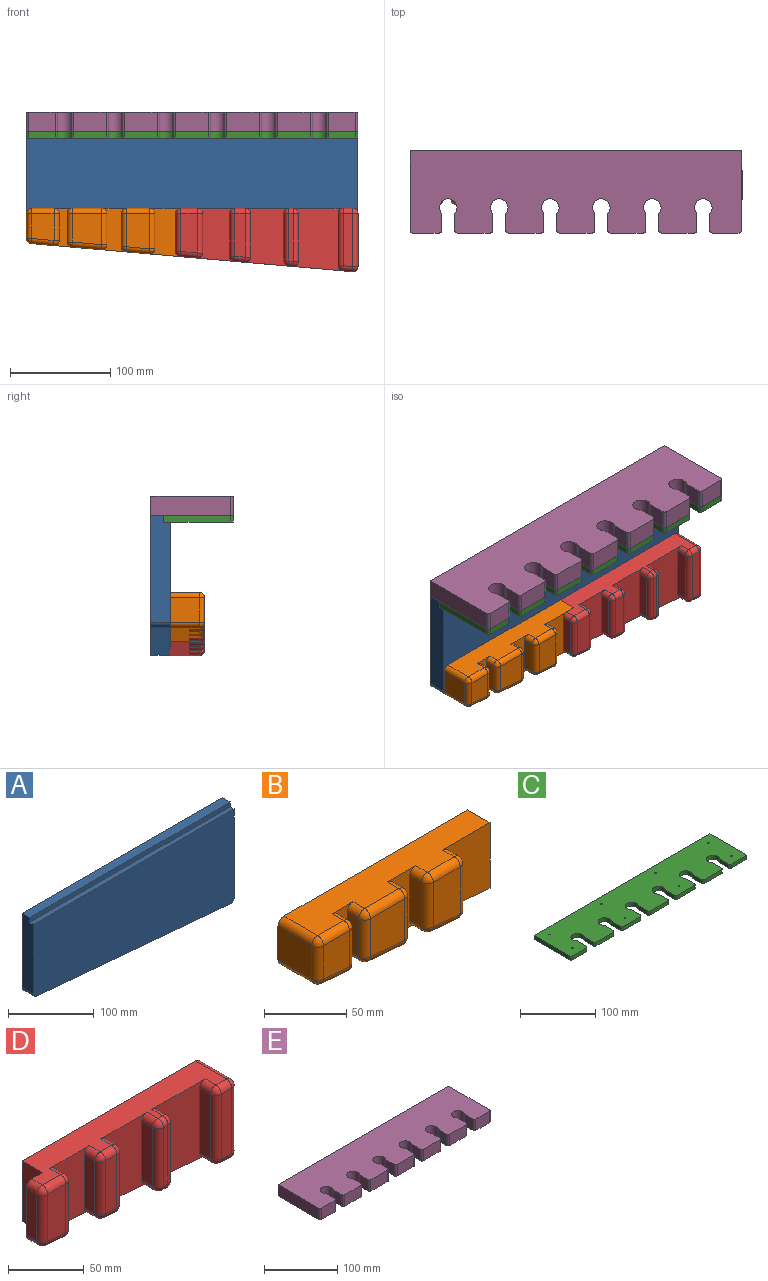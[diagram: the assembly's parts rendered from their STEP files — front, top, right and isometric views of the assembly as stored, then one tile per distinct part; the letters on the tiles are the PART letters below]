
ASSEMBLY  parts=5 mates=3
PART A: 10 faces, bbox 330.2x19.1x139.2 mm
  f0: plane 106.16x19.05mm, normal (-1,0,0), area 1978.7mm2, adj f2,f3,f4,f5,f6,f8
  f1: plane 134.16x19.05mm, normal (1,0,0), area 2512.1mm2, adj f2,f3,f4,f5,f6,f9
  f2: plane 330.2x12.7mm, normal (0,0,1), area 4193.5mm2, adj f0,f1,f3,f6
  f3: plane 330.2x139.24mm, normal (0,1,0), area 41348.1mm2, adj f0,f1,f2,f7,f8,f9
  f4: plane 330.2x132.38mm, normal (0,-1,0), area 39083.6mm2, adj f0,f1,f5,f7,f8,f9
  f5: plane 330.2x6.35mm, normal (0,0,1), area 2096.8mm2, adj f0,f1,f4,f6
  f6: plane 330.2x6.86mm, normal (0,-1,0), area 2264.5mm2, adj f0,f1,f2,f5
  f7: plane 320.04x28mm, normal (-0.09,0,-1), area 6120.1mm2, adj f3,f4,f8,f9
  f8: cylinder r=5.08mm len=19.05mm, axis (0,1,0), area 143.6mm2, adj f0,f3,f4,f7
  f9: cylinder r=5.08mm len=19.05mm, axis (0,-1,0), area 160.5mm2, adj f1,f3,f4,f7
PART B: 60 faces, bbox 163.5x34.1x48.9 mm
  f0: plane 29.06x24.88mm, normal (-1,0,0), area 722.8mm2, adj f6,f40,f42,f43
  f1: plane 48.92x19.05mm, normal (1,0,0), area 931.9mm2, adj f5,f6,f14,f15
  f2: plane 35.17x23.24mm, normal (0,-1,0), area 793.8mm2, adj f31,f32,f36,f37
  f3: plane 26.84x22.42mm, normal (0,-1,0), area 579.6mm2, adj f43,f44,f48,f49
  f4: plane 31x29.59mm, normal (0,-1,0), area 879.1mm2, adj f19,f20,f24,f25
  f5: plane 158.43x29.06mm, normal (0,0,1), area 3771.2mm2, adj f1,f6,f9,f12,f14,f16,f20,f21
  f6: plane 163.51x48.92mm, normal (0,1,0), area 6803.7mm2, adj f0,f1,f5,f15,f40,f42,f52,f54
  f7: plane 31x10.01mm, normal (1,0,0), area 310.3mm2, adj f9,f21,f25,f27
  f8: plane 33.14x10.01mm, normal (-1,0,0), area 331.6mm2, adj f9,f30,f36,f39
  f9: plane 43.28x24.83mm, normal (0,-1,0), area 623.3mm2, adj f5,f7,f8,f15,f21,f27,f30,f39
  f10: plane 26.84x10.01mm, normal (1,0,0), area 268.6mm2, adj f12,f45,f49,f51
  f11: plane 28.42x10.01mm, normal (-1,0,0), area 284.4mm2, adj f12,f16,f18,f19
  f12: plane 38.56x18.48mm, normal (0,-1,0), area 320mm2, adj f5,f10,f11,f15,f16,f18,f45,f51
  f13: plane 35.17x10.01mm, normal (1,0,0), area 352mm2, adj f14,f28,f32,f33
  f14: plane 48.92x41.21mm, normal (0,-1,0), area 1702.3mm2, adj f1,f5,f13,f15,f28,f33
  f15: plane 158.88x29.06mm, normal (-0.09,0,-1), area 3794.1mm2, adj f1,f6,f9,f12,f14,f18,f24,f27
  f16: cylinder r=5.08mm len=10.01mm, axis (0,1,0), area 79.9mm2, adj f5,f11,f12,f17
  f17: sphere r=5.08mm, area 40.5mm2, adj f16,f19,f20
  f18: cylinder r=5.08mm len=10.01mm, axis (0,-1,0), area 75.4mm2, adj f11,f12,f15,f22
  f19: cylinder r=5.08mm len=28.42mm, axis (0,0,-1), area 226.7mm2, adj f4,f11,f17,f22
  f20: cylinder r=5.08mm len=29.59mm, axis (-1,0,0), area 236.1mm2, adj f4,f5,f17,f23
  f21: cylinder r=5.08mm len=10.01mm, axis (0,1,0), area 79.9mm2, adj f5,f7,f9,f23
  f22: sphere r=5.08mm, area 38.3mm2, adj f18,f19,f24
  f23: sphere r=5.08mm, area 40.5mm2, adj f20,f21,f25
  f24: cylinder r=5.08mm len=30.03mm, axis (1,0,-0.09), area 237mm2, adj f4,f15,f22,f26
  f25: cylinder r=5.08mm len=31mm, axis (0,0,1), area 247.4mm2, adj f4,f7,f23,f26
  f26: sphere r=5.08mm, area 42.8mm2, adj f24,f25,f27
  f27: cylinder r=5.08mm len=10.01mm, axis (0,1,0), area 84.3mm2, adj f7,f9,f15,f26
  f28: cylinder r=5.08mm len=10.01mm, axis (0,1,0), area 79.9mm2, adj f5,f13,f14,f29
  f29: sphere r=5.08mm, area 40.5mm2, adj f28,f31,f32
  f30: cylinder r=5.08mm len=10.01mm, axis (0,1,0), area 79.9mm2, adj f5,f8,f9,f34
  f31: cylinder r=5.08mm len=23.24mm, axis (-1,0,0), area 185.5mm2, adj f2,f5,f29,f34
  f32: cylinder r=5.08mm len=35.17mm, axis (0,0,1), area 280.6mm2, adj f2,f13,f29,f35
  f33: cylinder r=5.08mm len=10.01mm, axis (0,1,0), area 84.3mm2, adj f13,f14,f15,f35
  f34: sphere r=5.08mm, area 40.5mm2, adj f30,f31,f36
  f35: sphere r=5.08mm, area 42.8mm2, adj f32,f33,f37
  f36: cylinder r=5.08mm len=33.14mm, axis (0,0,-1), area 264.4mm2, adj f2,f8,f34,f38
  f37: cylinder r=5.08mm len=23.68mm, axis (1,0,-0.09), area 186.2mm2, adj f2,f15,f35,f38
  f38: sphere r=5.08mm, area 38.3mm2, adj f36,f37,f39
  f39: cylinder r=5.08mm len=10.01mm, axis (0,-1,0), area 75.4mm2, adj f8,f9,f15,f38
  f40: cylinder r=5.08mm len=29.06mm, axis (0,1,0), area 231.9mm2, adj f0,f5,f6,f41
  f41: sphere r=5.08mm, area 40.5mm2, adj f40,f43,f44
  f42: cylinder r=5.08mm len=29.06mm, axis (0,1,0), area 219mm2, adj f0,f6,f15,f46
  f43: cylinder r=5.08mm len=24.88mm, axis (0,0,-1), area 198.5mm2, adj f0,f3,f41,f46
  f44: cylinder r=5.08mm len=22.42mm, axis (-1,0,0), area 178.9mm2, adj f3,f5,f41,f47
  f45: cylinder r=5.08mm len=10.01mm, axis (0,1,0), area 79.9mm2, adj f5,f10,f12,f47
  f46: sphere r=5.08mm, area 38.3mm2, adj f42,f43,f48
  f47: sphere r=5.08mm, area 40.5mm2, adj f44,f45,f49
  f48: cylinder r=5.08mm len=22.86mm, axis (1,0,-0.09), area 179.6mm2, adj f3,f15,f46,f50
  f49: cylinder r=5.08mm len=26.84mm, axis (0,0,1), area 214.2mm2, adj f3,f10,f47,f50
  f50: sphere r=5.08mm, area 42.8mm2, adj f48,f49,f51
  f51: cylinder r=5.08mm len=10.01mm, axis (0,1,0), area 84.3mm2, adj f10,f12,f15,f50
  f52: cylinder r=0.76mm len=12.7mm, axis (0,1,0), area 60.8mm2, adj f6,f53
  f53: plane 1.52x1.52mm, normal (0,1,0), area 1.8mm2, adj f52
  f54: cylinder r=0.76mm len=12.7mm, axis (0,1,0), area 60.8mm2, adj f6,f55
  f55: plane 1.52x1.52mm, normal (0,1,0), area 1.8mm2, adj f54
  f56: cylinder r=1.35mm len=12.7mm, axis (0,1,0), area 107.9mm2, adj f6,f57
  f57: plane 2.71x2.71mm, normal (0,1,0), area 5.7mm2, adj f56
  f58: cylinder r=1.35mm len=12.7mm, axis (0,1,0), area 107.9mm2, adj f6,f59
  f59: plane 2.71x2.71mm, normal (0,1,0), area 5.7mm2, adj f58
PART C: 52 faces, bbox 330.2x69.1x6.4 mm
  f0: cylinder r=8.74mm len=17.48mm, axis (0,0,1), area 254mm2, adj f1,f27,f28,f29
  f1: plane 17.11x6.35mm, normal (-1,0,0), area 108.6mm2, adj f0,f28,f29,f30
  f2: plane 32.56x6.35mm, normal (0,-1,0), area 206.8mm2, adj f28,f29,f30,f31
  f3: plane 17.11x6.35mm, normal (1,0,0), area 108.6mm2, adj f4,f28,f29,f31
  f4: cylinder r=8.74mm len=17.48mm, axis (0,0,1), area 254mm2, adj f3,f5,f28,f29
  f5: plane 17.11x6.35mm, normal (-1,0,0), area 108.6mm2, adj f4,f28,f29,f32
  f6: plane 32.56x6.35mm, normal (0,-1,0), area 206.8mm2, adj f28,f29,f32,f33
  f7: plane 17.11x6.35mm, normal (1,0,0), area 108.6mm2, adj f8,f28,f29,f33
  f8: cylinder r=8.74mm len=17.48mm, axis (0,0,1), area 254mm2, adj f7,f9,f28,f29
  f9: plane 17.11x6.35mm, normal (-1,0,0), area 108.6mm2, adj f8,f28,f29,f34
  f10: plane 32.56x6.35mm, normal (0,-1,0), area 206.8mm2, adj f28,f29,f34,f35
  f11: plane 17.11x6.35mm, normal (1,0,0), area 108.6mm2, adj f12,f28,f29,f35
  f12: cylinder r=8.74mm len=17.48mm, axis (0,0,1), area 254mm2, adj f11,f13,f28,f29
  f13: plane 17.11x6.35mm, normal (-1,0,0), area 108.6mm2, adj f12,f28,f29,f36
  f14: plane 26.44x6.35mm, normal (0,-1,0), area 167.9mm2, adj f28,f29,f36,f37
  f15: plane 66.52x6.35mm, normal (1,0,0), area 422.4mm2, adj f16,f28,f29,f37
  f16: plane 330.2x6.35mm, normal (0,1,0), area 2096.8mm2, adj f15,f17,f28,f29
  f17: plane 66.52x6.35mm, normal (-1,0,0), area 422.4mm2, adj f16,f28,f29,f38
  f18: plane 26.44x6.35mm, normal (0,-1,0), area 167.9mm2, adj f28,f29,f38,f39
  f19: plane 17.11x6.35mm, normal (1,0,0), area 108.6mm2, adj f20,f28,f29,f39
  f20: cylinder r=8.74mm len=17.48mm, axis (0,0,1), area 254mm2, adj f19,f21,f28,f29
  f21: plane 17.11x6.35mm, normal (-1,0,0), area 108.6mm2, adj f20,f28,f29,f40
  f22: plane 32.56x6.35mm, normal (0,-1,0), area 206.8mm2, adj f28,f29,f40,f41
  f23: plane 17.11x6.35mm, normal (1,0,0), area 108.6mm2, adj f24,f28,f29,f41
  f24: cylinder r=8.74mm len=17.48mm, axis (0,0,1), area 254mm2, adj f23,f25,f28,f29
  f25: plane 17.11x6.35mm, normal (-1,0,0), area 108.6mm2, adj f24,f28,f29,f42
  f26: plane 32.56x6.35mm, normal (0,-1,0), area 206.8mm2, adj f28,f29,f42,f43
  f27: plane 17.11x6.35mm, normal (1,0,0), area 108.6mm2, adj f0,f28,f29,f43
  f28: plane 330.2x69.06mm, normal (0,0,-1), area 19926.2mm2, adj f0,f1,f2,f3,f4,f5,f6,f7
  f29: plane 330.2x69.06mm, normal (0,0,1), area 19926.2mm2, adj f0,f1,f2,f3,f4,f5,f6,f7
  f30: cylinder r=2.54mm len=6.35mm, axis (0,0,1), area 25.3mm2, adj f1,f2,f28,f29
  f31: cylinder r=2.54mm len=6.35mm, axis (0,0,-1), area 25.3mm2, adj f2,f3,f28,f29
  f32: cylinder r=2.54mm len=6.35mm, axis (0,0,1), area 25.3mm2, adj f5,f6,f28,f29
  f33: cylinder r=2.54mm len=6.35mm, axis (0,0,-1), area 25.3mm2, adj f6,f7,f28,f29
  f34: cylinder r=2.54mm len=6.35mm, axis (0,0,1), area 25.3mm2, adj f9,f10,f28,f29
  f35: cylinder r=2.54mm len=6.35mm, axis (0,0,-1), area 25.3mm2, adj f10,f11,f28,f29
  f36: cylinder r=2.54mm len=6.35mm, axis (0,0,1), area 25.3mm2, adj f13,f14,f28,f29
  f37: cylinder r=2.54mm len=6.35mm, axis (0,0,-1), area 25.3mm2, adj f14,f15,f28,f29
  f38: cylinder r=2.54mm len=6.35mm, axis (0,0,-1), area 25.3mm2, adj f17,f18,f28,f29
  f39: cylinder r=2.54mm len=6.35mm, axis (0,0,-1), area 25.3mm2, adj f18,f19,f28,f29
  f40: cylinder r=2.54mm len=6.35mm, axis (0,0,1), area 25.3mm2, adj f21,f22,f28,f29
  f41: cylinder r=2.54mm len=6.35mm, axis (0,0,-1), area 25.3mm2, adj f22,f23,f28,f29
  f42: cylinder r=2.54mm len=6.35mm, axis (0,0,1), area 25.3mm2, adj f25,f26,f28,f29
  f43: cylinder r=2.54mm len=6.35mm, axis (0,0,-1), area 25.3mm2, adj f26,f27,f28,f29
  f44: cylinder r=1.13mm len=6.35mm, axis (0,0,-1), area 45.1mm2, adj f28,f29
  f45: cylinder r=1.13mm len=6.35mm, axis (0,0,-1), area 45.1mm2, adj f28,f29
  f46: cylinder r=1.13mm len=6.35mm, axis (0,0,-1), area 45.1mm2, adj f28,f29
  f47: cylinder r=1.13mm len=6.35mm, axis (0,0,-1), area 45.1mm2, adj f28,f29
  f48: cylinder r=1.13mm len=6.35mm, axis (0,0,-1), area 45.1mm2, adj f28,f29
  f49: cylinder r=1.13mm len=6.35mm, axis (0,0,-1), area 45.1mm2, adj f28,f29
  f50: cylinder r=1.13mm len=6.35mm, axis (0,0,-1), area 45.1mm2, adj f28,f29
  f51: cylinder r=1.13mm len=6.35mm, axis (0,0,-1), area 45.1mm2, adj f28,f29
PART D: 74 faces, bbox 181.8x34.1x63 mm
  f0: plane 39.34x16.89mm, normal (0,-1,0), area 652mm2, adj f59,f60,f64,f65
  f1: plane 47.67x4.19mm, normal (0,-1,0), area 199mm2, adj f35,f36,f40,f41
  f2: plane 43.5x10.54mm, normal (0,-1,0), area 453.7mm2, adj f23,f24,f28,f29
  f3: plane 171.64x29.06mm, normal (0,0,1), area 3492.3mm2, adj f4,f6,f10,f13,f16,f17,f20,f24
  f4: plane 48.92x19.05mm, normal (-1,0,0), area 931.9mm2, adj f3,f6,f17,f19
  f5: plane 52.88x29.06mm, normal (1,0,0), area 1536.5mm2, adj f6,f44,f48,f49
  f6: plane 166.69x63.04mm, normal (0,1,0), area 9339.7mm2, adj f3,f4,f5,f19,f44,f49,f68,f70
  f7: plane 52.88x9.72mm, normal (0,-1,0), area 509.6mm2, adj f47,f48,f52,f53
  f8: plane 43.5x10.01mm, normal (1,0,0), area 435.4mm2, adj f10,f25,f29,f31
  f9: plane 47.3x10.01mm, normal (-1,0,0), area 473.4mm2, adj f10,f34,f40,f43
  f10: plane 57.44x43.88mm, normal (0,-1,0), area 1871.8mm2, adj f3,f8,f9,f19,f25,f31,f34,f43
  f11: plane 47.67x10.01mm, normal (1,0,0), area 477.1mm2, adj f13,f32,f36,f37
  f12: plane 52.03x10.01mm, normal (-1,0,0), area 520.7mm2, adj f13,f46,f52,f55
  f13: plane 62.17x50.23mm, normal (0,-1,0), area 2400.9mm2, adj f3,f11,f12,f19,f32,f37,f46,f55
  f14: plane 39.34x10.01mm, normal (1,0,0), area 393.7mm2, adj f16,f61,f65,f67
  f15: plane 42.58x10.01mm, normal (-1,0,0), area 426.1mm2, adj f16,f20,f22,f23
  f16: plane 52.72x37.53mm, normal (0,-1,0), area 1399.2mm2, adj f3,f14,f15,f19,f20,f22,f61,f67
  f17: plane 48.92x15.11mm, normal (0,1,0), area 719.2mm2, adj f3,f4,f18,f19,f56,f58
  f18: plane 37.86x10.01mm, normal (-1,0,0), area 378.9mm2, adj f17,f56,f58,f59
  f19: plane 171.64x29.06mm, normal (-0.09,0,-1), area 3497.2mm2, adj f4,f6,f10,f13,f16,f17,f22,f28
  f20: cylinder r=5.08mm len=10.01mm, axis (0,1,0), area 79.9mm2, adj f3,f15,f16,f21
  f21: sphere r=5.08mm, area 40.5mm2, adj f20,f23,f24
  f22: cylinder r=5.08mm len=10.01mm, axis (0,-1,0), area 75.4mm2, adj f15,f16,f19,f26
  f23: cylinder r=5.08mm len=42.58mm, axis (0,0,-1), area 339.8mm2, adj f2,f15,f21,f26
  f24: cylinder r=5.08mm len=10.54mm, axis (-1,0,0), area 84.1mm2, adj f2,f3,f21,f27
  f25: cylinder r=5.08mm len=10.01mm, axis (0,-1,0), area 79.9mm2, adj f3,f8,f10,f27
  f26: sphere r=5.08mm, area 38.3mm2, adj f22,f23,f28
  f27: sphere r=5.08mm, area 40.5mm2, adj f24,f25,f29
  f28: cylinder r=5.08mm len=10.98mm, axis (1,0,-0.09), area 84.4mm2, adj f2,f19,f26,f30
  f29: cylinder r=5.08mm len=43.5mm, axis (0,0,1), area 347.1mm2, adj f2,f8,f27,f30
  f30: sphere r=5.08mm, area 42.8mm2, adj f28,f29,f31
  f31: cylinder r=5.08mm len=10.01mm, axis (0,1,0), area 84.3mm2, adj f8,f10,f19,f30
  f32: cylinder r=5.08mm len=10.01mm, axis (0,-1,0), area 79.9mm2, adj f3,f11,f13,f33
  f33: sphere r=5.08mm, area 40.5mm2, adj f32,f35,f36
  f34: cylinder r=5.08mm len=10.01mm, axis (0,1,0), area 79.9mm2, adj f3,f9,f10,f38
  f35: cylinder r=5.08mm len=5.08mm, axis (-1,0,0), area 33.4mm2, adj f1,f3,f33,f38
  f36: cylinder r=5.08mm len=47.67mm, axis (0,0,1), area 380.4mm2, adj f1,f11,f33,f39
  f37: cylinder r=5.08mm len=10.01mm, axis (0,1,0), area 84.3mm2, adj f11,f13,f19,f39
  f38: sphere r=5.08mm, area 40.5mm2, adj f34,f35,f40
  f39: sphere r=5.08mm, area 42.8mm2, adj f36,f37,f41
  f40: cylinder r=5.08mm len=47.3mm, axis (0,0,-1), area 377.5mm2, adj f1,f9,f38,f42
  f41: cylinder r=5.08mm len=5.43mm, axis (1,0,-0.09), area 33.6mm2, adj f1,f19,f39,f42
  f42: sphere r=5.08mm, area 38.3mm2, adj f40,f41,f43
  f43: cylinder r=5.08mm len=10.01mm, axis (0,-1,0), area 75.4mm2, adj f9,f10,f19,f42
  f44: cylinder r=5.08mm len=29.06mm, axis (0,1,0), area 231.9mm2, adj f3,f5,f6,f45
  f45: sphere r=5.08mm, area 40.5mm2, adj f44,f47,f48
  f46: cylinder r=5.08mm len=10.01mm, axis (0,1,0), area 79.9mm2, adj f3,f12,f13,f50
  f47: cylinder r=5.08mm len=9.72mm, axis (-1,0,0), area 77.5mm2, adj f3,f7,f45,f50
  f48: cylinder r=5.08mm len=52.88mm, axis (0,0,1), area 421.9mm2, adj f5,f7,f45,f51
  f49: cylinder r=5.08mm len=29.06mm, axis (0,-1,0), area 244.8mm2, adj f5,f6,f19,f51
  f50: sphere r=5.08mm, area 40.5mm2, adj f46,f47,f52
  f51: sphere r=5.08mm, area 42.8mm2, adj f48,f49,f53
  f52: cylinder r=5.08mm len=52.03mm, axis (0,0,-1), area 415.2mm2, adj f7,f12,f50,f54
  f53: cylinder r=5.08mm len=10.16mm, axis (1,0,-0.09), area 77.8mm2, adj f7,f19,f51,f54
  f54: sphere r=5.08mm, area 38.3mm2, adj f52,f53,f55
  f55: cylinder r=5.08mm len=10.01mm, axis (0,-1,0), area 75.4mm2, adj f12,f13,f19,f54
  f56: cylinder r=5.08mm len=10.01mm, axis (0,-1,0), area 79.9mm2, adj f3,f17,f18,f57
  f57: sphere r=5.08mm, area 40.5mm2, adj f56,f59,f60
  f58: cylinder r=5.08mm len=10.01mm, axis (0,-1,0), area 75.4mm2, adj f17,f18,f19,f62
  f59: cylinder r=5.08mm len=37.86mm, axis (0,0,-1), area 302.1mm2, adj f0,f18,f57,f62
  f60: cylinder r=5.08mm len=16.89mm, axis (-1,0,0), area 134.8mm2, adj f0,f3,f57,f63
  f61: cylinder r=5.08mm len=10.01mm, axis (0,-1,0), area 79.9mm2, adj f3,f14,f16,f63
  f62: sphere r=5.08mm, area 38.3mm2, adj f58,f59,f64
  f63: sphere r=5.08mm, area 40.5mm2, adj f60,f61,f65
  f64: cylinder r=5.08mm len=17.33mm, axis (1,0,-0.09), area 135.3mm2, adj f0,f19,f62,f66
  f65: cylinder r=5.08mm len=39.34mm, axis (0,0,1), area 313.9mm2, adj f0,f14,f63,f66
  f66: sphere r=5.08mm, area 42.8mm2, adj f64,f65,f67
  f67: cylinder r=5.08mm len=10.01mm, axis (0,1,0), area 84.3mm2, adj f14,f16,f19,f66
  f68: cylinder r=1.35mm len=12.7mm, axis (0,1,0), area 107.9mm2, adj f6,f69
  f69: plane 2.71x2.71mm, normal (0,1,0), area 5.7mm2, adj f68
  f70: cylinder r=1.35mm len=12.7mm, axis (0,1,0), area 107.9mm2, adj f6,f71
  f71: plane 2.71x2.71mm, normal (0,1,0), area 5.7mm2, adj f70
  f72: cylinder r=1.35mm len=12.7mm, axis (0,1,0), area 107.9mm2, adj f6,f73
  f73: plane 2.71x2.71mm, normal (0,1,0), area 5.7mm2, adj f72
PART E: 44 faces, bbox 330.2x81.8x19.1 mm
  f0: plane 19.05x17.11mm, normal (1,0,0), area 325.9mm2, adj f1,f28,f29,f43
  f1: cylinder r=8.74mm len=19.05mm, axis (0,0,1), area 762.1mm2, adj f0,f2,f28,f29
  f2: plane 19.05x17.11mm, normal (-1,0,0), area 325.9mm2, adj f1,f28,f29,f30
  f3: plane 32.56x19.05mm, normal (0,-1,0), area 620.3mm2, adj f28,f29,f30,f31
  f4: plane 19.05x17.11mm, normal (1,0,0), area 325.9mm2, adj f5,f28,f29,f31
  f5: cylinder r=8.74mm len=19.05mm, axis (0,0,1), area 762.1mm2, adj f4,f6,f28,f29
  f6: plane 19.05x17.11mm, normal (-1,0,0), area 325.9mm2, adj f5,f28,f29,f32
  f7: plane 32.56x19.05mm, normal (0,-1,0), area 620.3mm2, adj f28,f29,f32,f33
  f8: plane 19.05x17.11mm, normal (1,0,0), area 325.9mm2, adj f9,f28,f29,f33
  f9: cylinder r=8.74mm len=19.05mm, axis (0,0,1), area 762.1mm2, adj f8,f10,f28,f29
  f10: plane 19.05x17.11mm, normal (-1,0,0), area 325.9mm2, adj f9,f28,f29,f34
  f11: plane 32.56x19.05mm, normal (0,-1,0), area 620.3mm2, adj f28,f29,f34,f35
  f12: plane 19.05x17.11mm, normal (1,0,0), area 325.9mm2, adj f13,f28,f29,f35
  f13: cylinder r=8.74mm len=19.05mm, axis (0,0,1), area 762.1mm2, adj f12,f14,f28,f29
  f14: plane 19.05x17.11mm, normal (-1,0,0), area 325.9mm2, adj f13,f28,f29,f36
  f15: plane 32.56x19.05mm, normal (0,-1,0), area 620.3mm2, adj f28,f29,f36,f37
  f16: plane 19.05x17.11mm, normal (1,0,0), area 325.9mm2, adj f17,f28,f29,f37
  f17: cylinder r=8.74mm len=19.05mm, axis (0,0,1), area 762.1mm2, adj f16,f18,f28,f29
  f18: plane 19.05x17.11mm, normal (-1,0,0), area 325.9mm2, adj f17,f28,f29,f38
  f19: plane 26.44x19.05mm, normal (0,-1,0), area 503.7mm2, adj f28,f29,f38,f39
  f20: plane 79.22x19.05mm, normal (1,0,0), area 1509.2mm2, adj f21,f28,f29,f39
  f21: plane 330.2x19.05mm, normal (0,1,0), area 6290.3mm2, adj f20,f22,f28,f29
  f22: plane 79.22x19.05mm, normal (-1,0,0), area 1509.2mm2, adj f21,f28,f29,f40
  f23: plane 26.44x19.05mm, normal (0,-1,0), area 503.7mm2, adj f28,f29,f40,f41
  f24: plane 19.05x17.11mm, normal (1,0,0), area 325.9mm2, adj f25,f28,f29,f41
  f25: cylinder r=8.74mm len=19.05mm, axis (0,0,1), area 762.1mm2, adj f24,f26,f28,f29
  f26: plane 19.05x17.11mm, normal (-1,0,0), area 325.9mm2, adj f25,f28,f29,f42
  f27: plane 32.56x19.05mm, normal (0,-1,0), area 620.3mm2, adj f28,f29,f42,f43
  f28: plane 330.2x81.76mm, normal (0,0,-1), area 24151.9mm2, adj f0,f1,f2,f3,f4,f5,f6,f7
  f29: plane 330.2x81.76mm, normal (0,0,1), area 24151.9mm2, adj f0,f1,f2,f3,f4,f5,f6,f7
  f30: cylinder r=2.54mm len=19.05mm, axis (0,0,1), area 76mm2, adj f2,f3,f28,f29
  f31: cylinder r=2.54mm len=19.05mm, axis (0,0,-1), area 76mm2, adj f3,f4,f28,f29
  f32: cylinder r=2.54mm len=19.05mm, axis (0,0,1), area 76mm2, adj f6,f7,f28,f29
  f33: cylinder r=2.54mm len=19.05mm, axis (0,0,-1), area 76mm2, adj f7,f8,f28,f29
  f34: cylinder r=2.54mm len=19.05mm, axis (0,0,1), area 76mm2, adj f10,f11,f28,f29
  f35: cylinder r=2.54mm len=19.05mm, axis (0,0,-1), area 76mm2, adj f11,f12,f28,f29
  f36: cylinder r=2.54mm len=19.05mm, axis (0,0,1), area 76mm2, adj f14,f15,f28,f29
  f37: cylinder r=2.54mm len=19.05mm, axis (0,0,-1), area 76mm2, adj f15,f16,f28,f29
  f38: cylinder r=2.54mm len=19.05mm, axis (0,0,-1), area 76mm2, adj f18,f19,f28,f29
  f39: cylinder r=2.54mm len=19.05mm, axis (0,0,1), area 76mm2, adj f19,f20,f28,f29
  f40: cylinder r=2.54mm len=19.05mm, axis (0,0,1), area 76mm2, adj f22,f23,f28,f29
  f41: cylinder r=2.54mm len=19.05mm, axis (0,0,-1), area 76mm2, adj f23,f24,f28,f29
  f42: cylinder r=2.54mm len=19.05mm, axis (0,0,1), area 76mm2, adj f26,f27,f28,f29
  f43: cylinder r=2.54mm len=19.05mm, axis (0,0,-1), area 76mm2, adj f0,f27,f28,f29
PLACE A t=(-29.58,-9.75,-2.68)mm
PLACE B t=(-29.14,-43.88,-41.26)mm
PLACE C t=(-29.58,-47.06,66.91)mm
PLACE D t=(-29.14,-43.88,-41.26)mm
PLACE E t=(-29.58,-31.58,86.22)mm
MATE fastened C.f16 <-> A.f6  axis (0,1,0) through (-29.58,-3.4,63.74)mm
MATE fastened D.f4 <-> B.f1  axis (-1,0,0) through (-30.72,-19.27,-33.97)mm
MATE fastened E.f28 <-> A.f2  axis (0,0,1) through (135.52,9.3,67.17)mm
